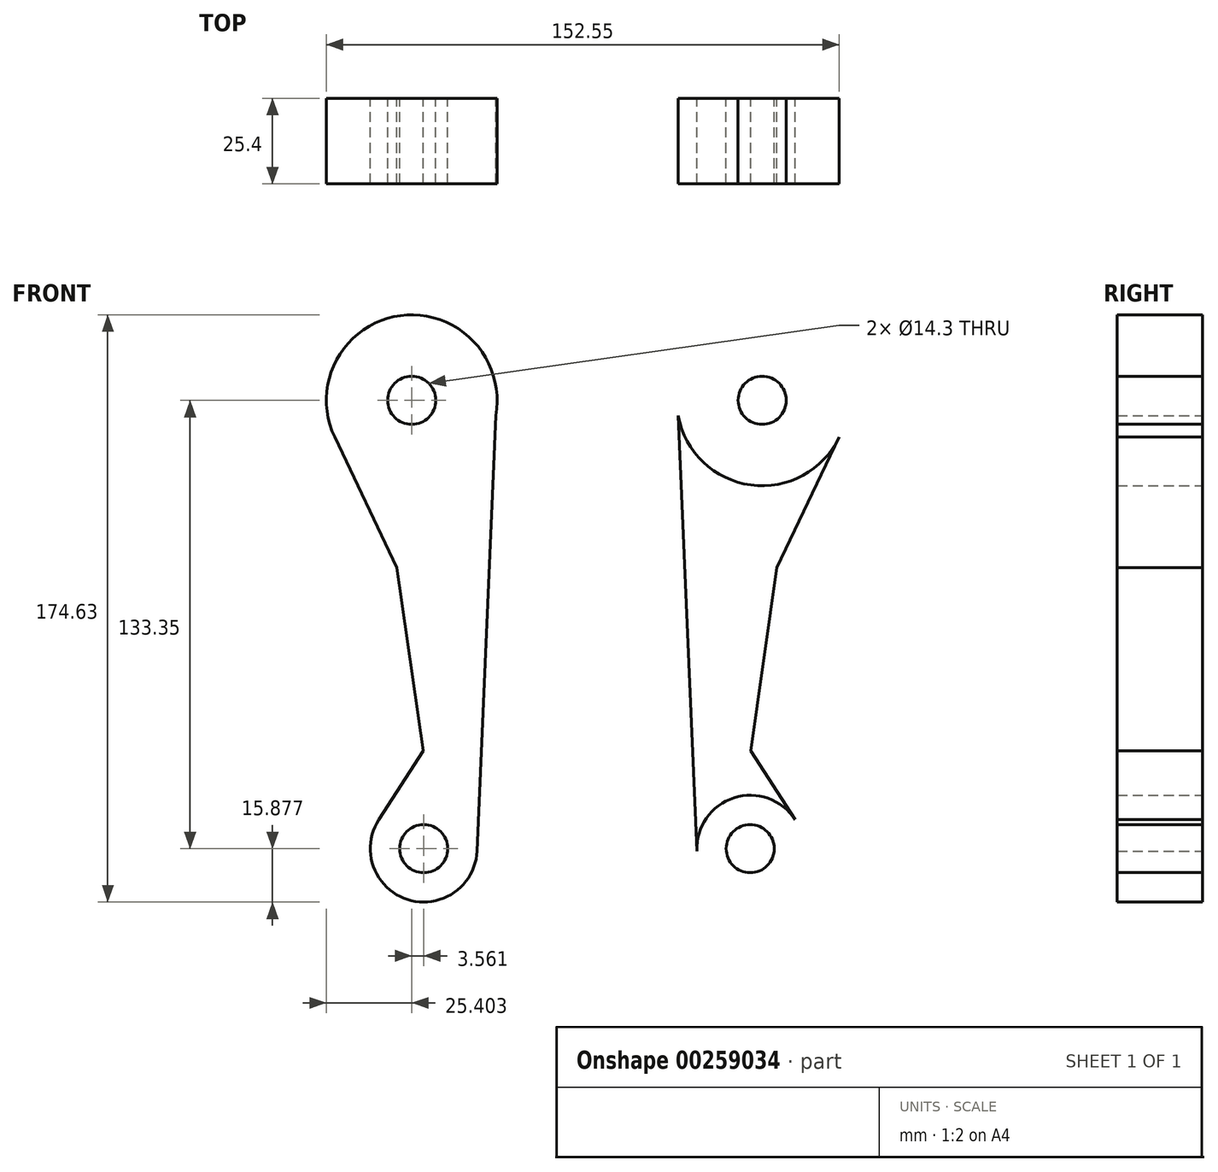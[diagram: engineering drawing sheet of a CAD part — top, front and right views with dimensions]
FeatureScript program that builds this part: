
annotation { "Feature Type Name" : "Feature", "Feature Type Description" : "" }
export const myFeature = defineFeature(function(context is Context, id is Id, definition is map)
    precondition{}
    {
        {
            var Q0;
            Q0=qCreatedBy(makeId("Front.planeOp"),FACE);
            var sketch = newSketch(context, id + "F0", { "sketchPlane" : qUnion([Q0])});
            skCircle(sketch, "E0", {"center": v(-52.12, 77.62) * mm, "radius": 25.4 * mm});
            skCircle(sketch, "E1", {"center": v(-48.56, -55.73) * mm, "radius": 15.88 * mm});
            skCircle(sketch, "E2", {"center": v(-52.12, 77.62) * mm, "radius": 7.15 * mm});
            skCircle(sketch, "E3", {"center": v(-48.56, -55.73) * mm, "radius": 7.15 * mm});
            skCircle(sketch, "E4.MirrorC", {"center": v(52.12, 77.62) * mm, "radius": 25.4 * mm});
            skCircle(sketch, "E5.MirrorC", {"center": v(48.56, -55.73) * mm, "radius": 15.88 * mm});
            skCircle(sketch, "E6.MirrorC", {"center": v(48.56, -55.73) * mm, "radius": 7.15 * mm});
            skCircle(sketch, "E7.MirrorC", {"center": v(52.12, 77.62) * mm, "radius": 7.15 * mm});
            skLineSegment(sketch, "E8", {"start": v(-61.89, -47.11) * mm, "end": v(-48.66, -26.66) * mm});
            skLineSegment(sketch, "E9", {"start": v(-48.66, -26.66) * mm, "end": v(-56.51, 27.9) * mm});
            skLineSegment(sketch, "E10", {"start": v(-56.51, 27.9) * mm, "end": v(-75.03, 66.66) * mm});
            skLineSegment(sketch, "E11", {"start": v(-26.83, 80.01) * mm, "end": v(-32.7, -56.41) * mm});
            skLineSegment(sketch, "E12.MirrorCS", {"start": v(26.83, 80.01) * mm, "end": v(32.7, -56.41) * mm});
            skLineSegment(sketch, "E13.MirrorCS", {"start": v(48.66, -26.66) * mm, "end": v(56.51, 27.9) * mm});
            skLineSegment(sketch, "E14.MirrorCS", {"start": v(56.51, 27.9) * mm, "end": v(75.03, 66.66) * mm});
            skLineSegment(sketch, "E15.MirrorCS", {"start": v(61.89, -47.11) * mm, "end": v(48.66, -26.66) * mm});
            skSolve(sketch);
        }
        {
            var Q0;
            {var subQ0=sQuery(id+"F0.wireOp",EDGE,"E8");Q0=makeQuery(id+"F0.imprint","IMPRINT",FACE,{"disambiguationData":[TD([[makeQuery(id+"F0.imprint","IMPRINT",EDGE,{"derivedFrom":subQ0}),-1.0]])]});}
            var Q1;
            Q1=makeQuery(id+"F0.imprint","IMPRINT",FACE,{"disambiguationData":[TD([[makeQuery(id+"F0.imprint","IMPRINT",EDGE,{"derivedFrom":sQuery(id+"F0.wireOp",EDGE,"E2")}),-1.0]])]});
            var Q2;
            Q2=makeQuery(id+"F0.imprint","IMPRINT",FACE,{"disambiguationData":[TD([[makeQuery(id+"F0.imprint","IMPRINT",EDGE,{"derivedFrom":sQuery(id+"F0.wireOp",EDGE,"E3")}),-1.0]])]});
            var Q3;
            Q3=makeQuery(id+"F0.imprint","IMPRINT",FACE,{"disambiguationData":[TD([[makeQuery(id+"F0.imprint","IMPRINT",EDGE,{"derivedFrom":sQuery(id+"F0.wireOp",EDGE,"E6.MirrorC")}),1.0]])]});
            var Q4;
            Q4=makeQuery(id+"F0.imprint","IMPRINT",FACE,{"disambiguationData":[TD([[makeQuery(id+"F0.imprint","IMPRINT",EDGE,{"derivedFrom":sQuery(id+"F0.wireOp",EDGE,"E13.MirrorCS")}),1.0]])]});
            var Q5;
            Q5=makeQuery(id+"F0.imprint","IMPRINT",FACE,{"disambiguationData":[TD([[makeQuery(id+"F0.imprint","IMPRINT",EDGE,{"derivedFrom":sQuery(id+"F0.wireOp",EDGE,"E7.MirrorC")}),1.0]])]});
            extrude(context, id + "F1", {"entities" : qUnion([Q0, Q1, Q2, Q3, Q4, Q5]), "depth" : 25.4 * mm});
        }
    });
